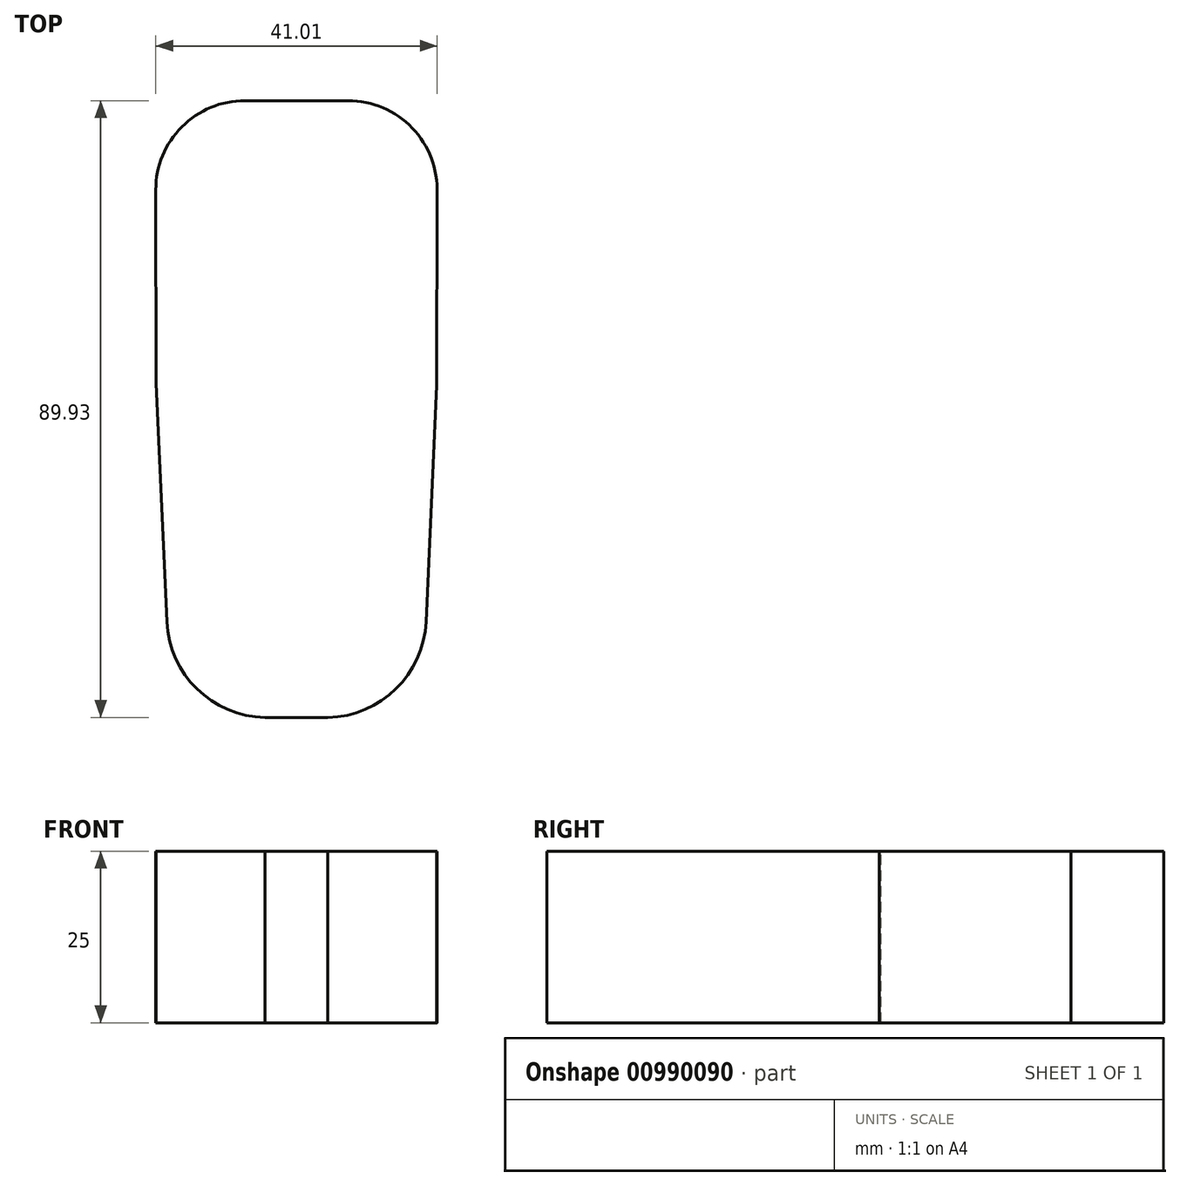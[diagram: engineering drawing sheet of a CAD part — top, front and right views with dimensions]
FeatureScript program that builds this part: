
annotation { "Feature Type Name" : "Feature", "Feature Type Description" : "" }
export const myFeature = defineFeature(function(context is Context, id is Id, definition is map)
    precondition{}
    {
        {
            var Q0;
            Q0=qCreatedBy(makeId("Top.planeOp"),FACE);
            var sketch = newSketch(context, id + "F0", { "sketchPlane" : qUnion([Q0])});
            skPoint(sketch, "E0.start.orphan", {"position": v(0, 0) * mm});
            skLineSegment(sketch, "E1.0", {"start": v(4.73, 87.82) * mm, "end": v(7.5, 87.82) * mm});
            skArc(sketch, "E1.1", {"start": v(20.48, 74.29) * mm, "mid": v(16.87, 83.82) * mm, "end": v(7.5, 87.82) * mm});
            skLineSegment(sketch, "E1.2", {"start": v(20.48, 74.28) * mm, "end": v(20.48, 74.29) * mm});
            skLineSegment(sketch, "E1.3", {"start": v(20.45, 46.33) * mm, "end": v(20.48, 74.28) * mm});
            skLineSegment(sketch, "E2.0", {"start": v(-4.75, 87.82) * mm, "end": v(-7.52, 87.82) * mm});
            skArc(sketch, "E3.0", {"start": v(-18.9, 11.87) * mm, "mid": v(-14.5, 2.05) * mm, "end": v(-4.59, -2.11) * mm});
            skLineSegment(sketch, "E3.1", {"start": v(-20.48, 46.6) * mm, "end": v(-18.9, 11.87) * mm});
            skLineSegment(sketch, "E3.2", {"start": v(-20.48, 46.6) * mm, "end": v(-20.52, 74.8) * mm});
            skArc(sketch, "E3.3", {"start": v(-7.52, 87.82) * mm, "mid": v(-16.71, 84) * mm, "end": v(-20.52, 74.8) * mm});
            skLineSegment(sketch, "E4.1", {"start": v(20.45, 46.33) * mm, "end": v(18.88, 11.87) * mm});
            skLineSegment(sketch, "E5", {"start": v(4.56, -2.11) * mm, "end": v(-4.59, -2.11) * mm});
            skLineSegment(sketch, "E6", {"start": v(4.73, 87.82) * mm, "end": v(-4.75, 87.82) * mm});
            skLineSegment(sketch, "E7", {"start": v(-0.01, 87.82) * mm, "end": v(-0.01, -15.61) * mm, "construction": true});
            skArc(sketch, "E8.MirrorCS", {"start": v(18.88, 11.87) * mm, "mid": v(14.48, 2.05) * mm, "end": v(4.56, -2.11) * mm});
            skSolve(sketch);
        }
        {
            var Q0;
            Q0 = qSketchRegion(id + "F0", true);
            var Q1;
            Q1=sQuery(id+"F0.wireOp",EDGE,"E2.0");
            var Q2;
            Q2=sQuery(id+"F0.wireOp",EDGE,"E5");
            var Q3;
            Q3=sQuery(id+"F0.wireOp",EDGE,"E1.2");
            var Q4;
            Q4=sQuery(id+"F0.wireOp",EDGE,"E6");
            var Q5;
            Q5=sQuery(id+"F0.wireOp",EDGE,"E1.0");
            var Q6;
            Q6=sQuery(id+"F0.wireOp",EDGE,"E1.1");
            var Q7;
            Q7=sQuery(id+"F0.wireOp",EDGE,"E1.3");
            var Q8;
            Q8=sQuery(id+"F0.wireOp",EDGE,"E4.1");
            var Q9;
            Q9=sQuery(id+"F0.wireOp",EDGE,"E3.0");
            var Q10;
            Q10=sQuery(id+"F0.wireOp",EDGE,"E3.1");
            var Q11;
            Q11=sQuery(id+"F0.wireOp",EDGE,"E3.2");
            var Q12;
            Q12=sQuery(id+"F0.wireOp",EDGE,"E3.3");
            var Q13;
            Q13=sQuery(id+"F0.wireOp",EDGE,"E8.MirrorCS");
            extrude(context, id + "F1", {"entities" : qUnion([Q0]), "bodyType" : ToolBodyType.SURFACE, "surfaceEntities" : qUnion([Q1, Q2, Q3, Q4, Q5, Q6, Q7, Q8, Q9, Q10, Q11, Q12, Q13]), "depth" : 25 * mm, "offsetDistance" : 25 * mm});
        }
    });
